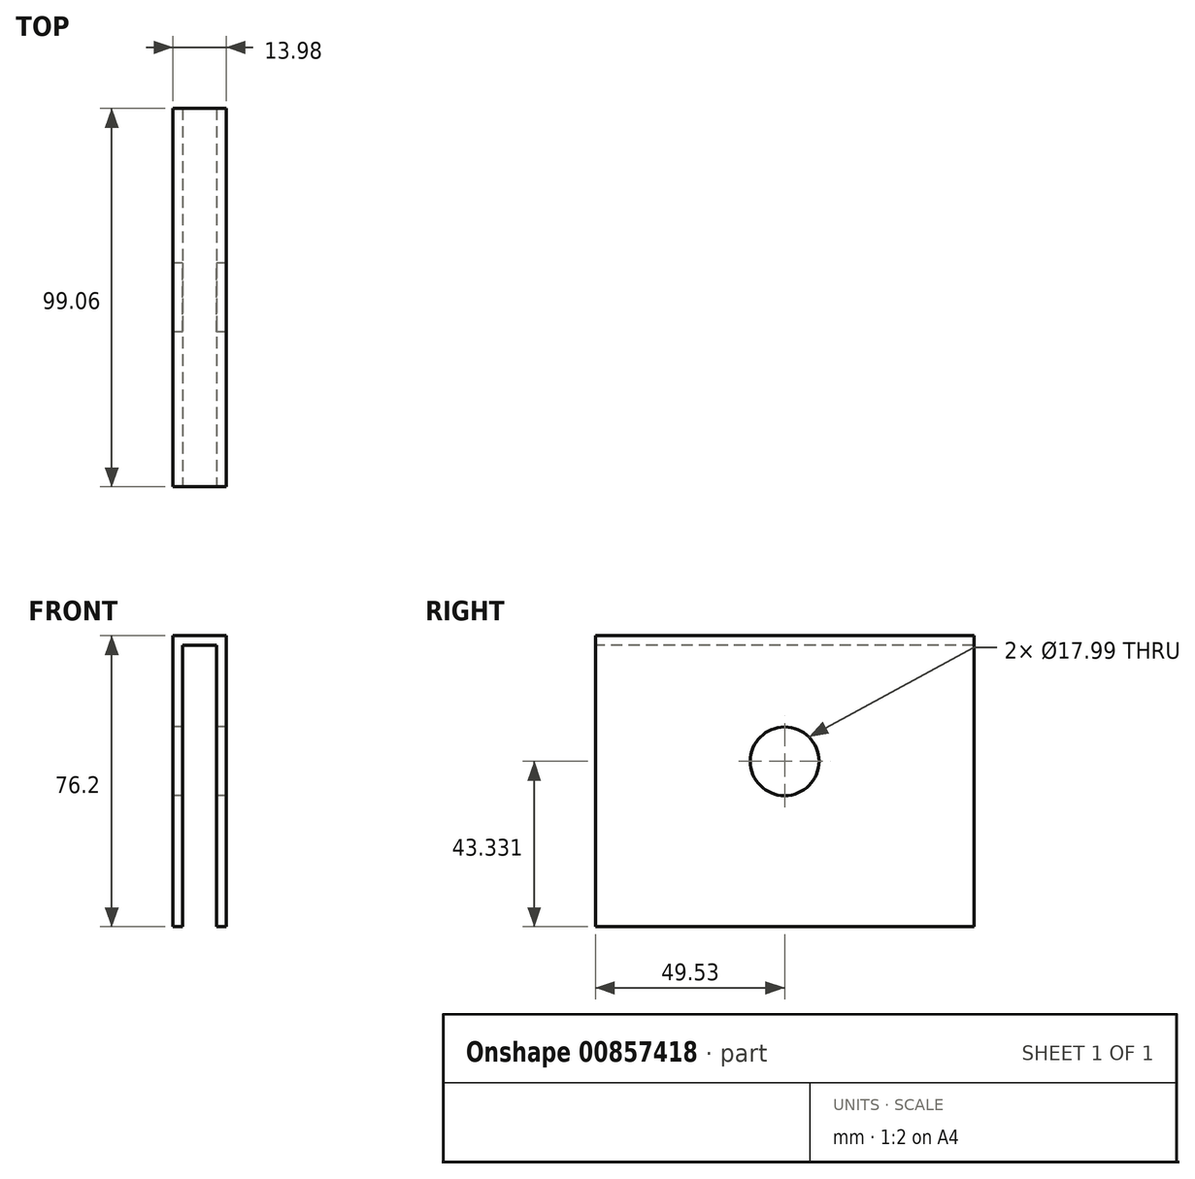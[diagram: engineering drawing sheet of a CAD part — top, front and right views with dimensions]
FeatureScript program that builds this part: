
annotation { "Feature Type Name" : "Feature", "Feature Type Description" : "" }
export const myFeature = defineFeature(function(context is Context, id is Id, definition is map)
    precondition{}
    {
        {
            var Q0;
            Q0=qCreatedBy(makeId("Top.planeOp"),FACE);
            var sketch = newSketch(context, id + "F0", { "sketchPlane" : qUnion([Q0])});
            skLineSegment(sketch, "E0.bottom", {"start": v(-6.99, 49.53) * mm, "end": v(6.98, 49.53) * mm});
            skLineSegment(sketch, "E0.top", {"start": v(-6.98, -49.53) * mm, "end": v(6.99, -49.53) * mm});
            skLineSegment(sketch, "E0.left", {"start": v(-6.99, 49.53) * mm, "end": v(-6.98, -49.53) * mm});
            skLineSegment(sketch, "E0.right", {"start": v(6.99, 49.53) * mm, "end": v(6.99, -49.53) * mm});
            skPoint(sketch, "E0.middle", {"position": v(0, 0) * mm});
            skSolve(sketch);
        }
        {
            var Q0;
            Q0=makeQuery(id+"F0.imprint","IMPRINT",FACE,{"disambiguationData":[TD([[makeQuery(id+"F0.imprint","IMPRINT",EDGE,{"derivedFrom":sQuery(id+"F0.wireOp",EDGE,"E0.bottom")}),-1.0]])]});
            extrude(context, id + "F1", {"entities" : qUnion([Q0]), "oppositeDirection" : true, "depth" : 76.2 * mm, "offsetDistance" : 25.4 * mm});
        }
        {
            var Q0;
            Q0=makeQuery(id+"F1.opExtrude","CAP_FACE",FACE,{"disambiguationData":[OSD([sQuery(id+"F0.wireOp",EDGE,"E0.bottom"),sQuery(id+"F0.wireOp",EDGE,"E0.top"),sQuery(id+"F0.wireOp",EDGE,"E0.left"),sQuery(id+"F0.wireOp",EDGE,"E0.right")])],"isStart":false});
            var Q1;
            Q1=makeQuery(id+"F1.opExtrude","SWEPT_FACE",FACE,{"disambiguationData":[OSD([sQuery(id+"F0.wireOp",EDGE,"E0.bottom")])]});
            var Q2;
            Q2=makeQuery(id+"F1.opExtrude","SWEPT_FACE",FACE,{"disambiguationData":[OSD([sQuery(id+"F0.wireOp",EDGE,"E0.top")])]});
            shell(context, id + "F2", {"entities" : qUnion([Q0, Q1, Q2]), "thickness" : 2.54 * mm});
        }
        {
            var Q0;
            Q0=makeQuery(id+"F1.opExtrude","SWEPT_FACE",FACE,{"disambiguationData":[OSD([sQuery(id+"F0.wireOp",EDGE,"E0.left")])]});
            var sketch = newSketch(context, id + "F3", { "sketchPlane" : qUnion([Q0])});
            skCircle(sketch, "E1", {"center": v(0, -32.87) * mm, "radius": 9 * mm});
            skSolve(sketch);
        }
        {
            var Q0;
            Q0=makeQuery(id+"F3.imprint","IMPRINT",FACE,{"disambiguationData":[TD([[makeQuery(id+"F3.imprint","IMPRINT",EDGE,{"derivedFrom":sQuery(id+"F3.wireOp",EDGE,"E1")}),1.0]])]});
            var Q1;
            Q1=sQuery(id+"F3.wireOp",EDGE,"E1");
            extrude(context, id + "F4", {"entities" : qUnion([Q0]), "operationType" : NewBodyOperationType.REMOVE, "surfaceEntities" : qUnion([Q1]), "oppositeDirection" : true, "depth" : 118.62 * mm, "offsetDistance" : 25.4 * mm});
        }
    });
